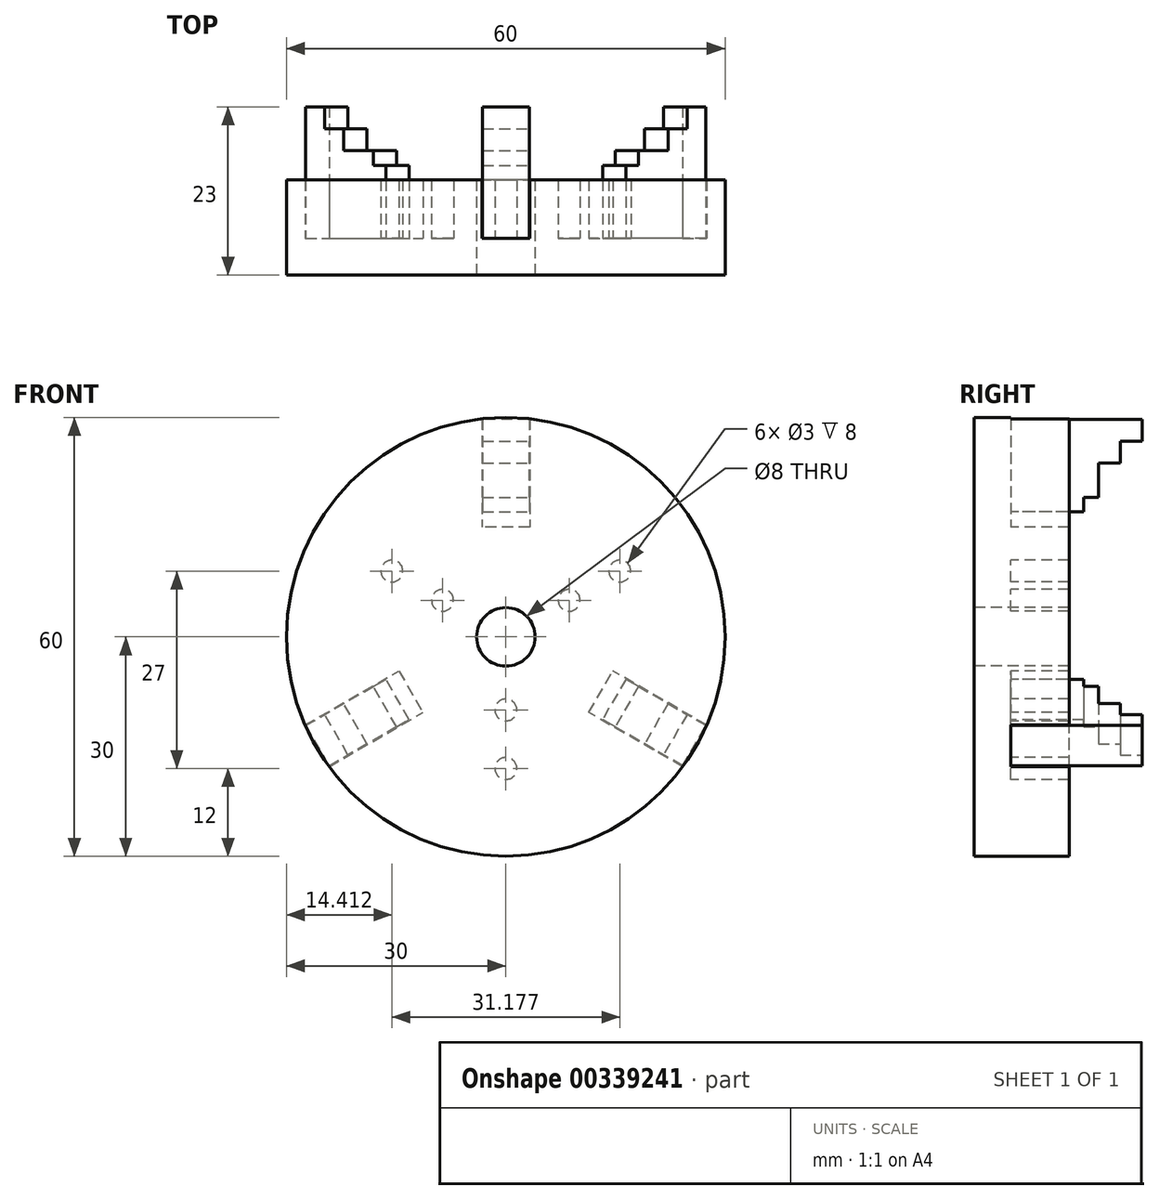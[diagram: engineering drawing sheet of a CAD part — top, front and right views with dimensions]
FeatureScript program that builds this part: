
annotation { "Feature Type Name" : "Feature", "Feature Type Description" : "" }
export const myFeature = defineFeature(function(context is Context, id is Id, definition is map)
    precondition{}
    {
        {
            var Q0;
            Q0=qCreatedBy(makeId("Front.planeOp"),FACE);
            var sketch = newSketch(context, id + "F0", { "sketchPlane" : qUnion([Q0])});
            skCircle(sketch, "E0", {"center": v(0, 0) * mm, "radius": 30 * mm});
            skLineSegment(sketch, "E1", {"start": v(3.29, 29.82) * mm, "end": v(3.29, 15) * mm});
            skLineSegment(sketch, "E2", {"start": v(0, 30) * mm, "end": v(0, 107.53) * mm, "construction": true});
            skLineSegment(sketch, "E3.MirrorCS", {"start": v(-3.29, 29.82) * mm, "end": v(-3.29, 15) * mm});
            skLineSegment(sketch, "E4", {"start": v(3.29, 15) * mm, "end": v(-3.29, 15) * mm});
            skPoint(sketch, "E5", {"position": v(0, 15) * mm});
            skLineSegment(sketch, "E6.0", {"start": v(-3.19, 29.82) * mm, "end": v(-3.19, 15.1) * mm});
            skLineSegment(sketch, "E6.1", {"start": v(3.19, 15.1) * mm, "end": v(-3.19, 15.1) * mm});
            skLineSegment(sketch, "E6.2", {"start": v(3.19, 29.82) * mm, "end": v(3.19, 15.1) * mm});
            skLineSegment(sketch, "E7.1.0", {"start": v(-27.47, -12.06) * mm, "end": v(-14.63, -4.65) * mm});
            skLineSegment(sketch, "E7.1.1", {"start": v(-27.42, -12.15) * mm, "end": v(-14.67, -4.8) * mm});
            skLineSegment(sketch, "E7.1.2", {"start": v(-14.67, -4.8) * mm, "end": v(-11.48, -10.3) * mm});
            skLineSegment(sketch, "E7.1.3", {"start": v(-24.23, -17.67) * mm, "end": v(-11.48, -10.3) * mm});
            skLineSegment(sketch, "E7.1.4", {"start": v(-14.63, -4.65) * mm, "end": v(-11.35, -10.35) * mm});
            skLineSegment(sketch, "E7.1.5", {"start": v(-24.18, -17.76) * mm, "end": v(-11.35, -10.35) * mm});
            skLineSegment(sketch, "E7.2.0", {"start": v(24.18, -17.76) * mm, "end": v(11.35, -10.35) * mm});
            skLineSegment(sketch, "E7.2.1", {"start": v(24.23, -17.67) * mm, "end": v(11.48, -10.3) * mm});
            skLineSegment(sketch, "E7.2.2", {"start": v(11.48, -10.3) * mm, "end": v(14.67, -4.8) * mm});
            skLineSegment(sketch, "E7.2.3", {"start": v(27.42, -12.15) * mm, "end": v(14.67, -4.8) * mm});
            skLineSegment(sketch, "E7.2.4", {"start": v(11.35, -10.35) * mm, "end": v(14.63, -4.65) * mm});
            skLineSegment(sketch, "E7.2.5", {"start": v(27.47, -12.06) * mm, "end": v(14.63, -4.65) * mm});
            skCircle(sketch, "E8", {"center": v(0, -10) * mm, "radius": 1.5 * mm});
            skCircle(sketch, "E9", {"center": v(0, -18) * mm, "radius": 1.5 * mm});
            skCircle(sketch, "E10.1.0", {"center": v(8.66, 5) * mm, "radius": 1.5 * mm});
            skCircle(sketch, "E10.1.1", {"center": v(15.59, 9) * mm, "radius": 1.5 * mm});
            skCircle(sketch, "E10.2.0", {"center": v(-8.66, 5) * mm, "radius": 1.5 * mm});
            skCircle(sketch, "E10.2.1", {"center": v(-15.59, 9) * mm, "radius": 1.5 * mm});
            skCircle(sketch, "E11", {"center": v(0, 0) * mm, "radius": 4 * mm});
            skLineSegment(sketch, "E12", {"start": v(3.19, 29.77) * mm, "end": v(-3.19, 29.77) * mm});
            skLineSegment(sketch, "E13", {"start": v(3.19, 17.1) * mm, "end": v(-3.19, 17.1) * mm});
            skSolve(sketch);
        }
        {
            var Q0;
            {var subQ5=sQuery(id+"F0.wireOp",EDGE,"E1");Q0=makeQuery(id+"F0.imprint","IMPRINT",FACE,{"disambiguationData":[TD([[makeQuery(id+"F0.imprint","IMPRINT",EDGE,{"derivedFrom":subQ5}),1.0]])]});}
            extrude(context, id + "F1", {"entities" : qUnion([Q0]), "oppositeDirection" : true, "depth" : 8 * mm});
        }
        {
            var Q0;
            Q0=qCreatedBy(makeId("Front.planeOp"),FACE);
            var sketch = newSketch(context, id + "F2", { "sketchPlane" : qUnion([Q0])});
            skCircle(sketch, "E14", {"center": v(0, 0) * mm, "radius": 30 * mm});
            skCircle(sketch, "E15", {"center": v(0, 0) * mm, "radius": 4 * mm});
            skSolve(sketch);
        }
        {
            var Q0;
            Q0 = qSketchRegion(id + "F2", true);
            extrude(context, id + "F3", {"entities" : qUnion([Q0]), "operationType" : NewBodyOperationType.ADD, "depth" : 5 * mm});
        }
        {
            var Q0;
            {var subQ0=sQuery(id+"F0.wireOp",EDGE,"E12");Q0=makeQuery(id+"F0.imprint","IMPRINT",FACE,{"disambiguationData":[TD([[makeQuery(id+"F0.imprint","IMPRINT",EDGE,{"derivedFrom":subQ0}),1.0]])]});}
            extrude(context, id + "F4", {"entities" : qUnion([Q0]), "oppositeDirection" : true, "depth" : 18 * mm});
        }
        {
            var Q0;
            Q0=qCreatedBy(makeId("Right.planeOp"),FACE);
            var sketch = newSketch(context, id + "F5", { "sketchPlane" : qUnion([Q0])});
            skPoint(sketch, "E16.start.orphan", {"position": v(-3.87, 29.77) * mm});
            skPoint(sketch, "E17", {"position": v(18, 29.77) * mm});
            skPoint(sketch, "E18", {"position": v(18, 17.1) * mm});
            skPoint(sketch, "E19", {"position": v(0, 17.1) * mm});
            skLineSegment(sketch, "E20", {"start": v(18, 29.77) * mm, "end": v(18, 26.77) * mm});
            skLineSegment(sketch, "E21", {"start": v(18, 26.77) * mm, "end": v(15, 26.77) * mm});
            skLineSegment(sketch, "E22", {"start": v(15, 26.77) * mm, "end": v(15, 23.77) * mm});
            skLineSegment(sketch, "E23", {"start": v(15, 23.77) * mm, "end": v(12, 23.77) * mm});
            skLineSegment(sketch, "E24", {"start": v(12, 23.77) * mm, "end": v(12, 17.1) * mm});
            skLineSegment(sketch, "E25", {"start": v(12, 17.1) * mm, "end": v(18, 17.1) * mm});
            skLineSegment(sketch, "E26", {"start": v(18, 17.1) * mm, "end": v(18, 26.77) * mm});
            skLineSegment(sketch, "E27.bottom", {"start": v(12, 17.1) * mm, "end": v(10, 17.1) * mm});
            skLineSegment(sketch, "E27.top", {"start": v(12, 19.1) * mm, "end": v(10, 19.1) * mm});
            skLineSegment(sketch, "E27.left", {"start": v(12, 17.1) * mm, "end": v(12, 19.1) * mm});
            skLineSegment(sketch, "E27.right", {"start": v(10, 17.1) * mm, "end": v(10, 19.1) * mm});
            skSolve(sketch);
        }
        {
            var Q0;
            Q0=makeQuery(id+"F5.imprint","IMPRINT",FACE,{"disambiguationData":[TD([[makeQuery(id+"F5.imprint","IMPRINT",EDGE,{"derivedFrom":sQuery(id+"F5.wireOp",EDGE,"E21")}),1.0]])]});
            var Q1;
            Q1=makeQuery(id+"F5.imprint","IMPRINT",FACE,{"disambiguationData":[TD([[makeQuery(id+"F5.imprint","IMPRINT",EDGE,{"derivedFrom":sQuery(id+"F5.wireOp",EDGE,"E27.bottom")}),-1.0]])]});
            extrude(context, id + "F6", {"entities" : qUnion([Q0, Q1]), "operationType" : NewBodyOperationType.REMOVE, "endBound" : BoundingType.SYMMETRIC, "oppositeDirection" : true, "depth" : 25 * mm});
        }
        {
            var Q0;
            Q0=qCreatedBy(makeId("Right.planeOp"),FACE);
            var sketch = newSketch(context, id + "F7", { "sketchPlane" : qUnion([Q0])});
            skLineSegment(sketch, "E28", {"start": v(0, 0) * mm, "end": v(64.44, 0) * mm});
            skSolve(sketch);
        }
        {
            var Q0;
            Q0=makeQuery(id+"F4.opExtrude","SWEPT_BODY",BODY,{"disambiguationData":[OSD([sQuery(id+"F0.wireOp",EDGE,"E6.0"),sQuery(id+"F0.wireOp",EDGE,"E6.1"),sQuery(id+"F0.wireOp",EDGE,"E6.2"),sQuery(id+"F0.wireOp",EDGE,"E12")])]});
            var Q1;
            Q1=sQuery(id+"F7.wireOp",EDGE,"E28");
            circularPattern(context, id + "F8", {"entities" : qUnion([Q0]), "axis" : qUnion([Q1]), "angle" : 360 * degree, "instanceCount" : 3, "equalSpace" : true});
        }
    });
